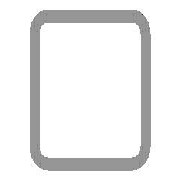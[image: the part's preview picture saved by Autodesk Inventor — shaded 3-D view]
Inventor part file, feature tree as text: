
AUTODESK INVENTOR PART (.ipt)
format: ipt  version: 2025 (Build 290162010, 162A)  size: 134,144 bytes
history: native  units: mm (DEFAULTED — no unit token found)
features: other x4, sketch x1, plane x1
ambient origin geometry x8: Origin, YZ Plane, XZ Plane, XY Plane, X Axis, Y Axis, Z Axis, Center Point
bodies: Solid1 (feature_tree), Body (feature_tree)
feature tree (6):
  parser-record x1  (decoder bookkeeping rows leaked as tree rows — omitted from the tree; the rows remain in map.json)
  other  "Driven Length"
  other  "Start Plane"
  other  "End Plane"
  sketch  "Sketch3"  dims[d3=3000.0mm d4=0.0mm d7=4.0mm d9=40.0mm d11=40.0mm d12=2.0mm d13=-0.0mm d14=3000.0mm d15=20.0mm d16=20.0mm d17=90.0deg d18=3000.0mm]
  plane  "Work Plane3"
